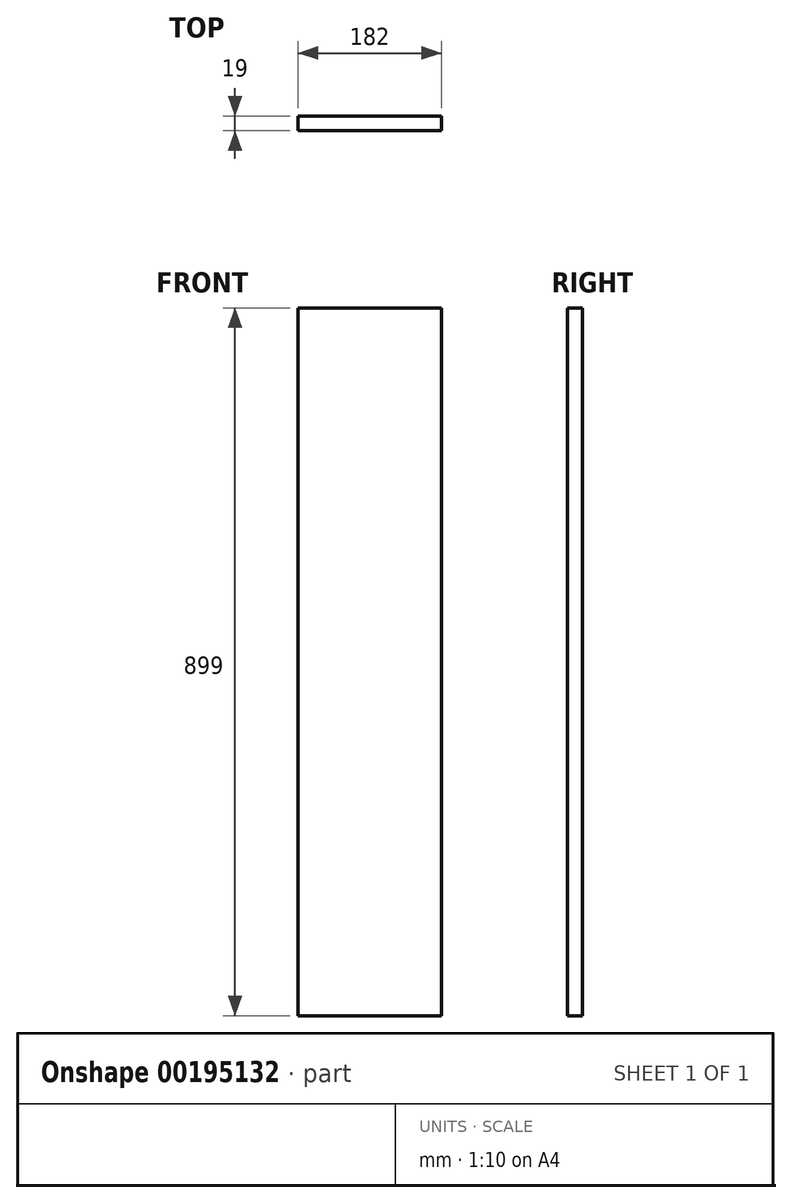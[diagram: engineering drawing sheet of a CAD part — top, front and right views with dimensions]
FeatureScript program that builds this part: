
annotation { "Feature Type Name" : "Feature", "Feature Type Description" : "" }
export const myFeature = defineFeature(function(context is Context, id is Id, definition is map)
    precondition{}
    {
        {
            var Q0;
            Q0=qCreatedBy(makeId("Front.planeOp"),FACE);
            var sketch = newSketch(context, id + "F0", { "sketchPlane" : qUnion([Q0])});
            skLineSegment(sketch, "E0.bottom", {"start": v(-92.93, 688.84) * mm, "end": v(89.07, 688.84) * mm});
            skLineSegment(sketch, "E0.top", {"start": v(-92.93, -210.16) * mm, "end": v(89.07, -210.16) * mm});
            skLineSegment(sketch, "E0.left", {"start": v(-92.93, 688.84) * mm, "end": v(-92.93, -210.16) * mm});
            skLineSegment(sketch, "E0.right", {"start": v(89.07, 688.84) * mm, "end": v(89.07, -210.16) * mm});
            skSolve(sketch);
        }
        {
            var Q0;
            Q0 = qSketchRegion(id + "F0", true);
            extrude(context, id + "F1", {"entities" : qUnion([Q0]), "depth" : 19 * mm});
        }
    });
